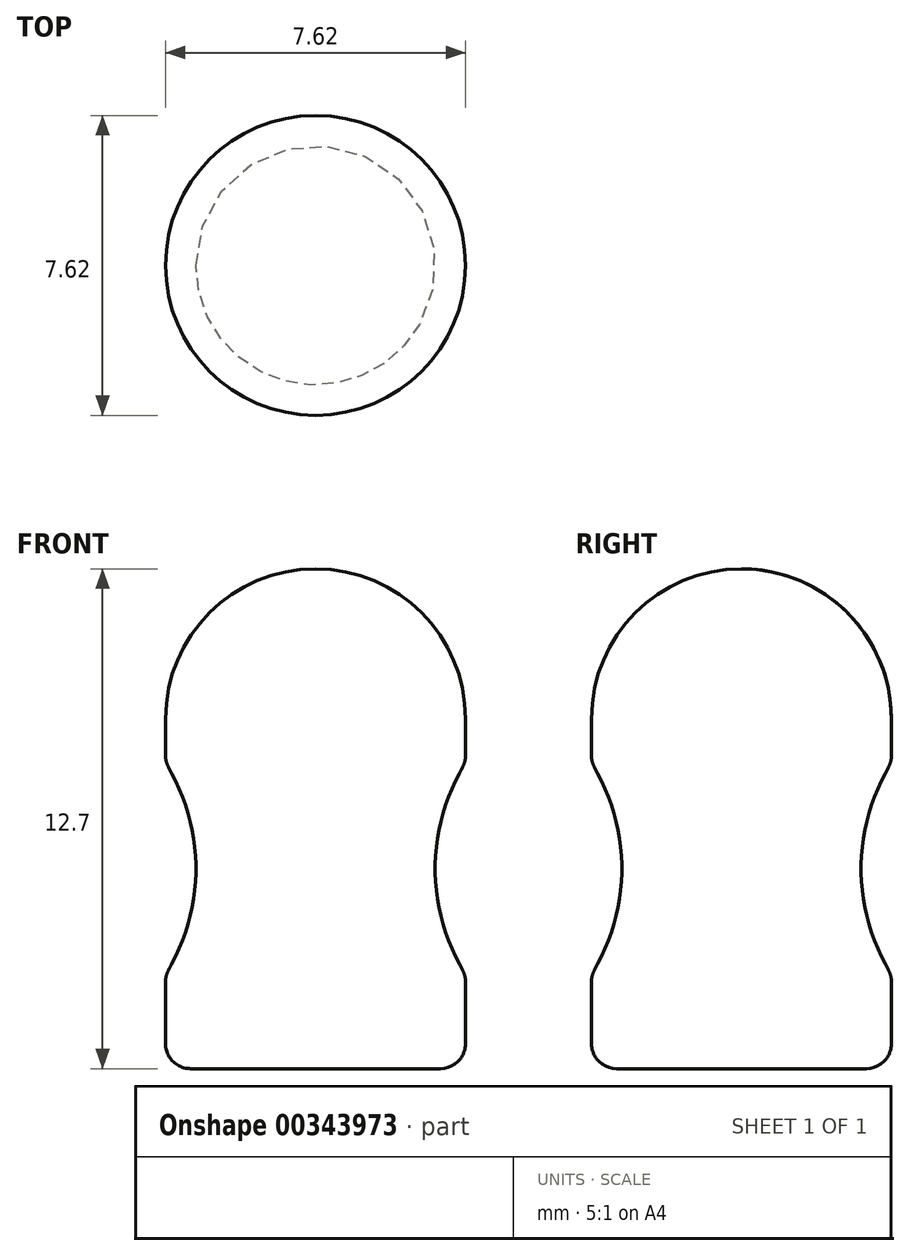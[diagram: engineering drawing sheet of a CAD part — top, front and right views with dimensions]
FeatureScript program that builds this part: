
annotation { "Feature Type Name" : "Feature", "Feature Type Description" : "" }
export const myFeature = defineFeature(function(context is Context, id is Id, definition is map)
    precondition{}
    {
        {
            var Q0;
            Q0=qCreatedBy(makeId("Right.planeOp"),FACE);
            var sketch = newSketch(context, id + "F0", { "sketchPlane" : qUnion([Q0])});
            skLineSegment(sketch, "E0.bottom", {"start": v(0, 0) * mm, "end": v(-3.81, 0) * mm});
            skLineSegment(sketch, "E0.top", {"start": v(0, 12.7) * mm, "end": v(0, 12.7) * mm});
            skLineSegment(sketch, "E0.left", {"start": v(0, 0) * mm, "end": v(0, 12.7) * mm});
            skLineSegment(sketch, "E0.right", {"start": v(-3.81, 0) * mm, "end": v(-3.81, 2.37) * mm});
            skPoint(sketch, "E1.visualSharp", {"position": v(-3.81, 12.7) * mm});
            skArc(sketch, "E1.filletArc", {"start": v(0, 12.7) * mm, "mid": v(-2.7, 11.58) * mm, "end": v(-3.81, 8.9) * mm});
            skLineSegment(sketch, "E2", {"start": v(-3.81, 7.8) * mm, "end": v(-3.65, 7.5) * mm});
            skLineSegment(sketch, "E3", {"start": v(-3.65, 2.66) * mm, "end": v(-3.81, 2.37) * mm});
            skLineSegment(sketch, "E4.trimOffspring", {"start": v(-3.81, 7.8) * mm, "end": v(-3.81, 8.9) * mm});
            skPoint(sketch, "E5.visualSharp", {"position": v(-2.34, 5.08) * mm});
            skArc(sketch, "E5.filletArc", {"start": v(-3.65, 2.66) * mm, "mid": v(-3.04, 5.08) * mm, "end": v(-3.65, 7.5) * mm});
            skSolve(sketch);
        }
        {
            var Q0;
            Q0=makeQuery(id+"F0.imprint","IMPRINT",FACE,{"disambiguationData":[TD([[makeQuery(id+"F0.imprint","IMPRINT",EDGE,{"derivedFrom":sQuery(id+"F0.wireOp",EDGE,"E0.bottom")}),-1.0]])]});
            var Q1;
            Q1=sQuery(id+"F0.wireOp",EDGE,"E0.left");
            revolve(context, id + "F1", {"entities" : qUnion([Q0]), "axis" : qUnion([Q1]), "revolveType" : RevolveType.FULL});
        }
        {
            var Q0;
            Q0=makeQuery(id+"F1.opRevolve","SWEPT_EDGE",EDGE,{"disambiguationData":[OSD([sQuery(id+"F0.wireOp",EDGE,"E0.bottom"),sQuery(id+"F0.wireOp",EDGE,"E0.right")])]});
            var Q1;
            Q1=makeQuery(id+"F1.opRevolve","SWEPT_EDGE",EDGE,{"disambiguationData":[OSD([sQuery(id+"F0.wireOp",EDGE,"E0.right"),sQuery(id+"F0.wireOp",EDGE,"E3")])]});
            var Q2;
            Q2=makeQuery(id+"F1.opRevolve","SWEPT_EDGE",EDGE,{"disambiguationData":[OSD([sQuery(id+"F0.wireOp",EDGE,"E2"),sQuery(id+"F0.wireOp",EDGE,"E4.trimOffspring")])]});
            fillet(context, id + "F2", {"entities" : qUnion([Q0, Q1, Q2]), "radius" : 0.64 * mm, "tangentPropagation" : true, "allowEdgeOverflow" : false});
        }
    });
